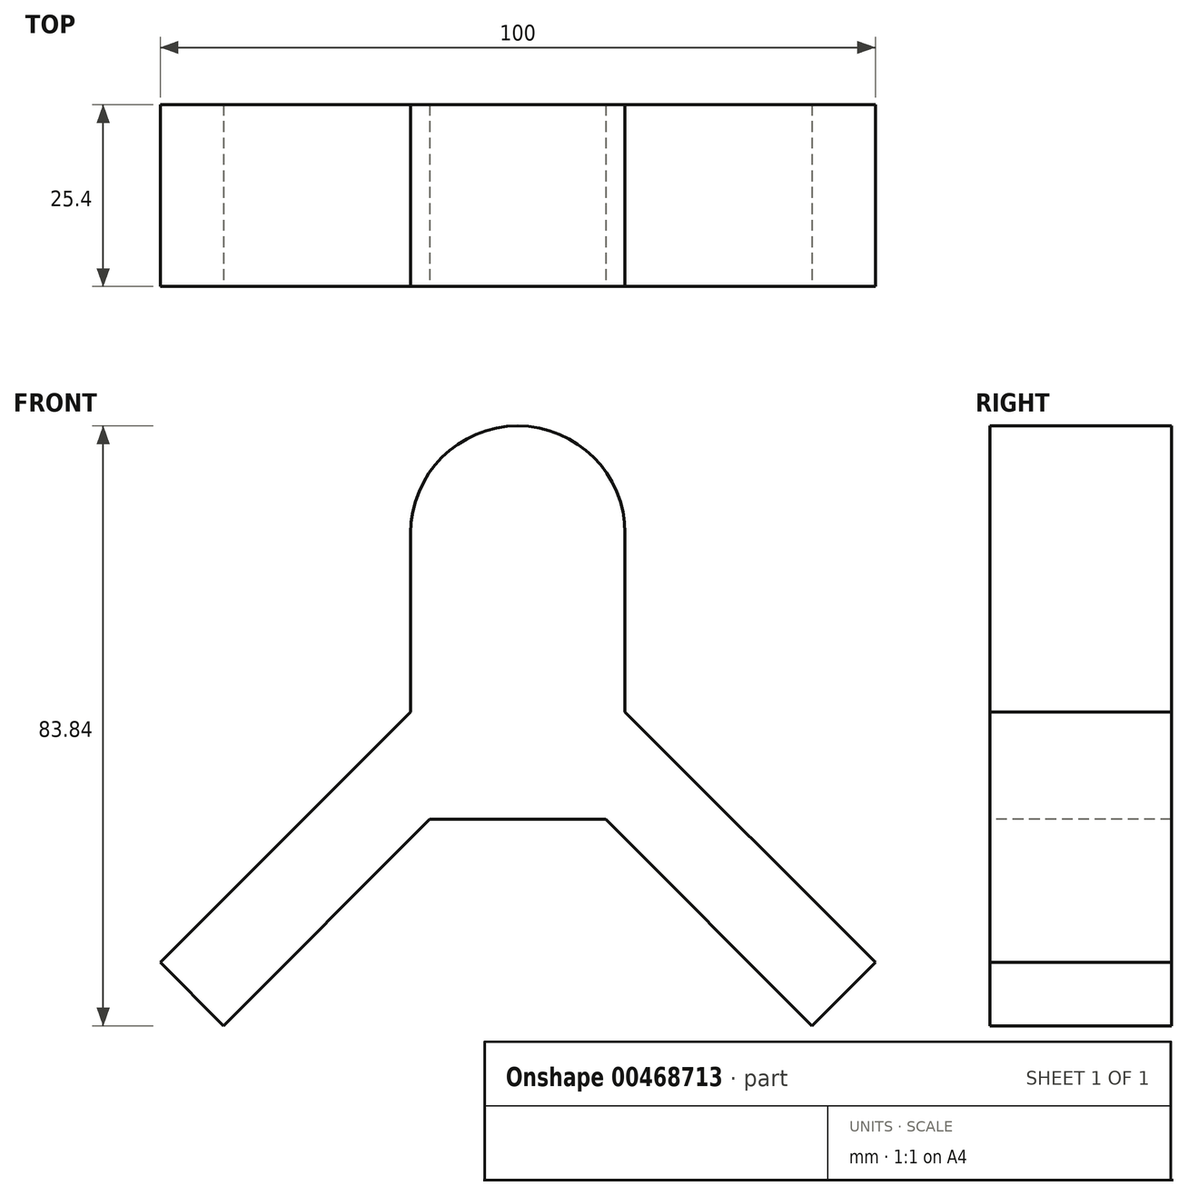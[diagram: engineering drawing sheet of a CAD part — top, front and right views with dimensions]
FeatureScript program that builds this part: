
annotation { "Feature Type Name" : "Feature", "Feature Type Description" : "" }
export const myFeature = defineFeature(function(context is Context, id is Id, definition is map)
    precondition{}
    {
        {
            var Q0;
            Q0=qCreatedBy(makeId("Front.planeOp"),FACE);
            var sketch = newSketch(context, id + "F0", { "sketchPlane" : qUnion([Q0])});
            skCircle(sketch, "E0", {"center": v(0, 35) * mm, "radius": 12.5 * mm});
            skArc(sketch, "E1", {"start": v(15, 35) * mm, "mid": v(0, 50) * mm, "end": v(-15, 35) * mm});
            skLineSegment(sketch, "E2", {"start": v(-15, 35) * mm, "end": v(-15, 10) * mm});
            skLineSegment(sketch, "E3", {"start": v(15, 35) * mm, "end": v(15, 10) * mm});
            skLineSegment(sketch, "E4", {"start": v(-15, 10) * mm, "end": v(-50, -25) * mm});
            skLineSegment(sketch, "E5", {"start": v(-50, -25) * mm, "end": v(-41.16, -33.84) * mm});
            skLineSegment(sketch, "E6.MirrorCS", {"start": v(15, 10) * mm, "end": v(50, -25) * mm});
            skLineSegment(sketch, "E7.MirrorCS", {"start": v(50, -25) * mm, "end": v(41.16, -33.84) * mm});
            skPoint(sketch, "E8.end.orphan", {"position": v(0, 3.66) * mm});
            skLineSegment(sketch, "E9", {"start": v(-41.16, -33.84) * mm, "end": v(-12.32, -5) * mm});
            skLineSegment(sketch, "E10", {"start": v(-12.32, -5) * mm, "end": v(0, -5) * mm});
            skLineSegment(sketch, "E11.MirrorCS", {"start": v(12.32, -5) * mm, "end": v(0, -5) * mm});
            skLineSegment(sketch, "E12.MirrorCS", {"start": v(41.16, -33.84) * mm, "end": v(12.32, -5) * mm});
            skLineSegment(sketch, "E13", {"start": v(0, 35) * mm, "end": v(-30.44, 35) * mm, "construction": true});
            skLineSegment(sketch, "E14.MirrorCS", {"start": v(0, 35) * mm, "end": v(30.44, 35) * mm, "construction": true});
            skSolve(sketch);
        }
        {
            var Q0;
            Q0=makeQuery(id+"F0.imprint","IMPRINT",FACE,{"disambiguationData":[TD([[makeQuery(id+"F0.imprint","IMPRINT",EDGE,{"derivedFrom":sQuery(id+"F0.wireOp",EDGE,"E0")}),1.0]])]});
            var Q1;
            Q1=makeQuery(id+"F0.imprint","IMPRINT",FACE,{"disambiguationData":[TD([[makeQuery(id+"F0.imprint","IMPRINT",EDGE,{"derivedFrom":sQuery(id+"F0.wireOp",EDGE,"E0")}),-1.0]])]});
            extrude(context, id + "F1", {"entities" : qUnion([Q0, Q1]), "oppositeDirection" : true, "depth" : 25.4 * mm});
        }
    });
